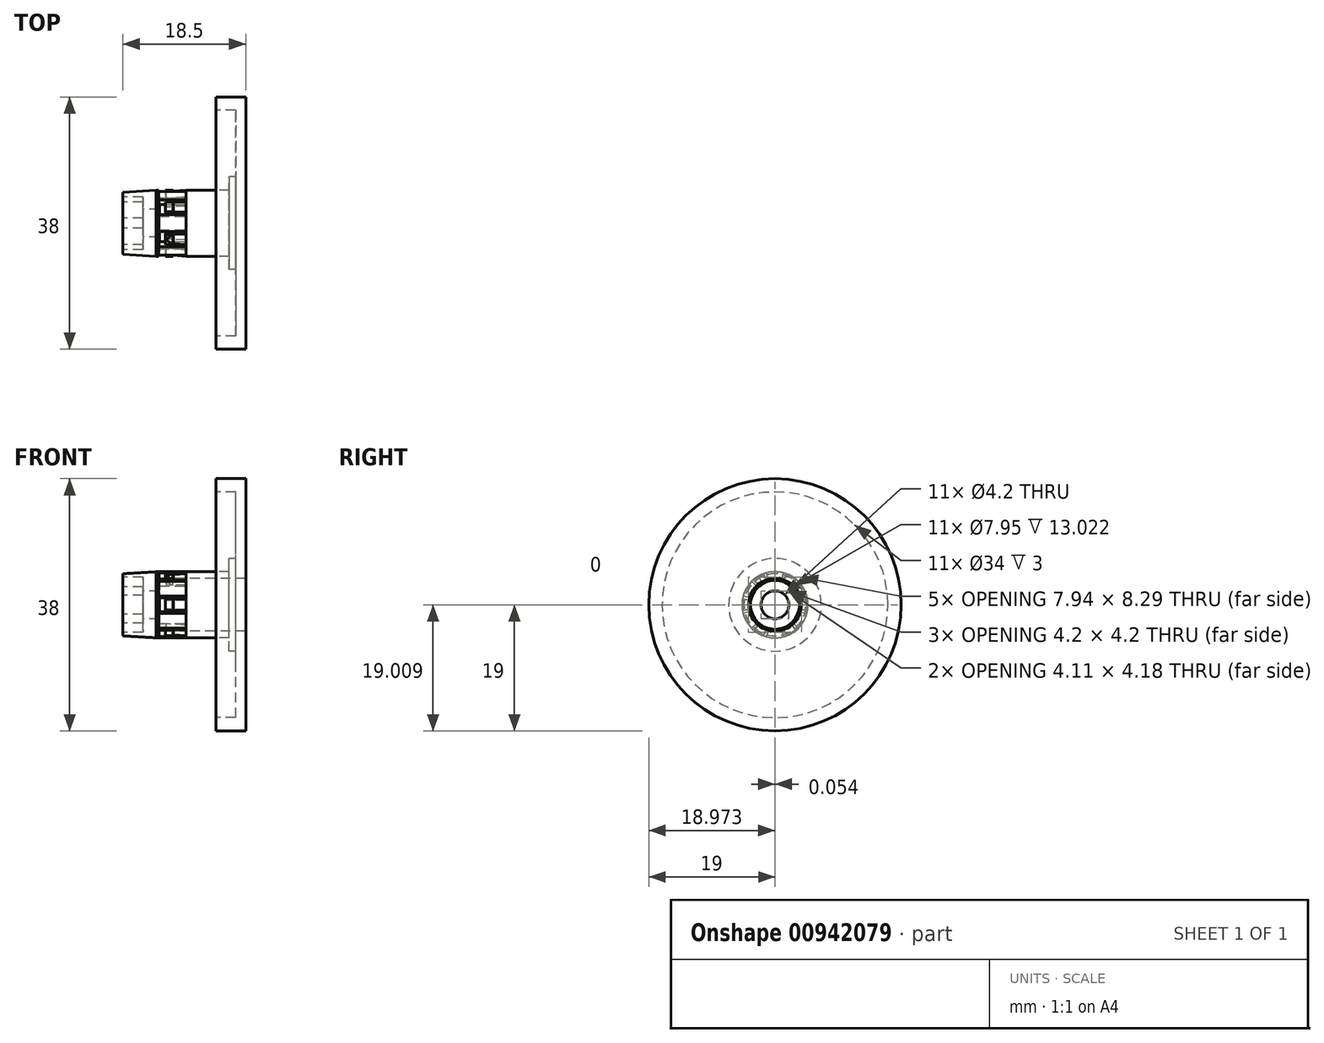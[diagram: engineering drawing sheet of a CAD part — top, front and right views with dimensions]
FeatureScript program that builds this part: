
annotation { "Feature Type Name" : "Feature", "Feature Type Description" : "" }
export const myFeature = defineFeature(function(context is Context, id is Id, definition is map)
    precondition{}
    {
        {
            var Q0;
            Q0=qCreatedBy(makeId("Top.planeOp"),FACE);
            var sketch = newSketch(context, id + "F0", { "sketchPlane" : qUnion([Q0])});
            skLineSegment(sketch, "E0", {"start": v(0, 19) * mm, "end": v(-4.5, 19) * mm});
            skLineSegment(sketch, "E1", {"start": v(-4.5, 19) * mm, "end": v(-4.5, 17) * mm});
            skLineSegment(sketch, "E2", {"start": v(-4.5, 17) * mm, "end": v(-1.5, 17) * mm});
            skLineSegment(sketch, "E3", {"start": v(-1.5, 17) * mm, "end": v(-1.5, 6.97) * mm});
            skLineSegment(sketch, "E4", {"start": v(-2.5, 4.97) * mm, "end": v(-18.5, 4.98) * mm});
            skLineSegment(sketch, "E5", {"start": v(-9, 3.97) * mm, "end": v(0, 3.97) * mm});
            skLineSegment(sketch, "E6", {"start": v(0, 19) * mm, "end": v(0, 3.97) * mm});
            skPoint(sketch, "E7.visualSharp", {"position": v(-1.5, 4.97) * mm});
            skLineSegment(sketch, "E8", {"start": v(-2.5, 4.97) * mm, "end": v(-2.5, 6.97) * mm});
            skLineSegment(sketch, "E9", {"start": v(-2.5, 6.97) * mm, "end": v(-1.5, 6.97) * mm});
            skLineSegment(sketch, "E10", {"start": v(-18.5, 2.1) * mm, "end": v(-13, 2.1) * mm});
            skLineSegment(sketch, "E11", {"start": v(-9, 3.97) * mm, "end": v(-13, 3.67) * mm});
            skLineSegment(sketch, "E12", {"start": v(-13, 3.67) * mm, "end": v(-13, 2.1) * mm});
            skLineSegment(sketch, "E13", {"start": v(-18.5, 2.1) * mm, "end": v(-18.5, 4.97) * mm});
            skLineSegment(sketch, "E14", {"start": v(-9, 3.97) * mm, "end": v(-9, 4.97) * mm});
            skLineSegment(sketch, "E15", {"start": v(-13, 3.67) * mm, "end": v(-13.1, 4.97) * mm});
            skLineSegment(sketch, "E16", {"start": v(0, 0) * mm, "end": v(12.8, 0) * mm, "construction": true});
            skLineSegment(sketch, "E17", {"start": v(-9, 4.97) * mm, "end": v(-12.1, 4.97) * mm});
            skLineSegment(sketch, "E18", {"start": v(-12.1, 4.97) * mm, "end": v(-12, 3.75) * mm});
            skLineSegment(sketch, "E19", {"start": v(-9, 4.97) * mm, "end": v(-10.92, 4.83) * mm});
            skLineSegment(sketch, "E20", {"start": v(-10.92, 4.83) * mm, "end": v(-10.93, 4.97) * mm});
            skSolve(sketch);
        }
        {
            var Q0;
            Q0=makeQuery(id+"F0.imprint","IMPRINT",FACE,{"disambiguationData":[TD([[makeQuery(id+"F0.imprint","IMPRINT",EDGE,{"derivedFrom":sQuery(id+"F0.wireOp",EDGE,"E0")}),1.0]])]});
            var Q1;
            Q1=makeQuery(id+"F0.imprint","IMPRINT",FACE,{"disambiguationData":[TD([[makeQuery(id+"F0.imprint","IMPRINT",EDGE,{"derivedFrom":sQuery(id+"F0.wireOp",EDGE,"E10")}),1.0]])]});
            var Q2;
            Q2=sQuery(id+"F0.wireOp",EDGE,"E16");
            revolve(context, id + "F1", {"surfaceOperationType" : NewSurfaceOperationType.NEW, "entities" : qUnion([Q0, Q1]), "axis" : qUnion([Q2]), "revolveType" : RevolveType.FULL});
        }
        {
            var Q0;
            {var subQ0=sQuery(id+"F0.wireOp",EDGE,"E18");Q0=makeQuery(id+"F0.imprint","IMPRINT",FACE,{"disambiguationData":[TD([[makeQuery(id+"F0.imprint","IMPRINT",EDGE,{"derivedFrom":subQ0}),1.0]])]});}
            var Q1;
            Q1=sQuery(id+"F0.wireOp",EDGE,"E16");
            revolve(context, id + "F2", {"operationType" : NewBodyOperationType.ADD, "surfaceOperationType" : NewSurfaceOperationType.NEW, "entities" : qUnion([Q0]), "axis" : qUnion([Q1]), "revolveType" : RevolveType.SYMMETRIC, "angle" : 20 * degree});
        }
        {
            var Q0;
            Q0=makeQuery(id+"F1.opRevolve","SWEPT_FACE",FACE,{"disambiguationData":[OSD([sQuery(id+"F0.wireOp",EDGE,"E14")])]});
            var sketch = newSketch(context, id + "F3", { "sketchPlane" : qUnion([Q0])});
            skLineSegment(sketch, "E21", {"start": v(-3.84, -1.03) * mm, "end": v(-4.8, -1.29) * mm});
            skLineSegment(sketch, "E22", {"start": v(-2.81, -2.81) * mm, "end": v(-3.52, -3.52) * mm});
            skPoint(sketch, "E23", {"position": v(0, 0) * mm});
            skArc(sketch, "E24", {"start": v(-2.81, -2.81) * mm, "mid": v(-3.44, -1.99) * mm, "end": v(-3.84, -1.03) * mm});
            skArc(sketch, "E25", {"start": v(-3.52, -3.52) * mm, "mid": v(-4.3, -2.49) * mm, "end": v(-4.8, -1.29) * mm});
            skSolve(sketch);
        }
        {
            var Q0;
            Q0=makeQuery(id+"F3.imprint","IMPRINT",FACE,{"disambiguationData":[TD([[makeQuery(id+"F3.imprint","IMPRINT",EDGE,{"derivedFrom":sQuery(id+"F3.wireOp",EDGE,"E21")}),1.0]])]});
            extrude(context, id + "F4", {"entities" : qUnion([Q0]), "operationType" : NewBodyOperationType.ADD, "endBound" : BoundingType.UP_TO_NEXT, "depth" : 25 * mm, "offsetDistance" : 25 * mm});
        }
        {
            var Q0;
            Q0=makeQuery(id+"F1.opRevolve","SWEPT_EDGE",EDGE,{"disambiguationData":[OSD([sQuery(id+"F0.wireOp",EDGE,"E4"),sQuery(id+"F0.wireOp",EDGE,"E13")])]});
            chamfer(context, id + "F5", {"entities" : qUnion([Q0]), "chamferType" : ChamferType.TWO_OFFSETS, "width1" : .3 * mm, "oppositeDirection" : false, "width2" : 5 * mm, "tangentPropagation" : true});
        }
        {
            var Q0;
            Q0=makeQuery(id+"F1.opRevolve","SWEPT_BODY",BODY,{"disambiguationData":[OSD([sQuery(id+"F0.wireOp",EDGE,"E0"),sQuery(id+"F0.wireOp",EDGE,"E1"),sQuery(id+"F0.wireOp",EDGE,"E2"),sQuery(id+"F0.wireOp",EDGE,"E3"),sQuery(id+"F0.wireOp",EDGE,"E4"),sQuery(id+"F0.wireOp",EDGE,"E5"),sQuery(id+"F0.wireOp",EDGE,"E6"),sQuery(id+"F0.wireOp",EDGE,"E8"),sQuery(id+"F0.wireOp",EDGE,"E9"),sQuery(id+"F0.wireOp",EDGE,"E14")])]});
            var Q1;
            Q1=sQuery(id+"F0.wireOp",EDGE,"E16");
            circularPattern(context, id + "F6", {"entities" : qUnion([Q0]), "axis" : qUnion([Q1]), "angle" : 360 * degree, "instanceCount" : 6, "equalSpace" : true, "isCentered" : true});
        }
        {
            var Q0;
            Q0=makeQuery(id+"F1.opRevolve","SWEPT_FACE",FACE,{"disambiguationData":[OSD([sQuery(id+"F0.wireOp",EDGE,"E13")])]});
            var sketch = newSketch(context, id + "F7", { "sketchPlane" : qUnion([Q0])});
            skCircle(sketch, "E26.cCircle", {"center": v(0, 0) * mm, "radius": 3.65 * mm, "construction": true});
            skLineSegment(sketch, "E26.0", {"start": v(3.97, -1.41) * mm, "end": v(0.76, -4.15) * mm});
            skLineSegment(sketch, "E26.1", {"start": v(0.76, -4.15) * mm, "end": v(-3.2, -2.73) * mm});
            skLineSegment(sketch, "E26.2", {"start": v(-3.2, -2.73) * mm, "end": v(-3.97, 1.41) * mm});
            skLineSegment(sketch, "E26.3", {"start": v(-3.97, 1.41) * mm, "end": v(-0.76, 4.15) * mm});
            skLineSegment(sketch, "E26.4", {"start": v(-0.76, 4.15) * mm, "end": v(3.2, 2.73) * mm});
            skLineSegment(sketch, "E26.5", {"start": v(3.2, 2.73) * mm, "end": v(3.97, -1.41) * mm});
            skPoint(sketch, "E26.0.midPoint", {"position": v(2.37, -2.78) * mm});
            skSolve(sketch);
        }
        {
            var Q0;
            Q0=makeQuery(id+"F7.imprint","IMPRINT",FACE,{"disambiguationData":[TD([[makeQuery(id+"F7.imprint","IMPRINT",EDGE,{"derivedFrom":sQuery(id+"F7.wireOp",EDGE,"E26.0")}),-1.0]])]});
            extrude(context, id + "F8", {"entities" : qUnion([Q0]), "operationType" : NewBodyOperationType.REMOVE, "oppositeDirection" : true, "depth" : 3 * mm, "offsetDistance" : 25 * mm});
        }
        {
            var Q0;
            Q0=makeQuery(id+"F1.opRevolve","SWEPT_EDGE",EDGE,{"disambiguationData":[OSD([sQuery(id+"F0.wireOp",EDGE,"E4"),sQuery(id+"F0.wireOp",EDGE,"E13")])]});
            var Q1;
            Q1=makeQuery(id+"F6.opPattern","COPY",EDGE,{"derivedFrom":makeQuery(id+"F4.opExtrude","CAP_EDGE",EDGE,{"disambiguationData":[OSD([sQuery(id+"F3.wireOp",EDGE,"E22")])],"isStart":false}),"instanceName":"-1"});
            var Q2;
            Q2=makeQuery(id+"F6.opPattern","COPY",EDGE,{"derivedFrom":makeQuery(id+"F4.opExtrude","CAP_EDGE",EDGE,{"disambiguationData":[OSD([sQuery(id+"F3.wireOp",EDGE,"E21")])],"isStart":false}),"instanceName":"-2"});
            var Q3;
            Q3=makeQuery(id+"F6.opPattern","COPY",EDGE,{"derivedFrom":makeQuery(id+"F4.opExtrude","CAP_EDGE",EDGE,{"disambiguationData":[OSD([sQuery(id+"F3.wireOp",EDGE,"E21")])],"isStart":false}),"instanceName":"-1"});
            var Q4;
            Q4=makeQuery(id+"F4.opExtrude","CAP_EDGE",EDGE,{"disambiguationData":[OSD([sQuery(id+"F3.wireOp",EDGE,"E22")])],"isStart":false});
            var Q5;
            Q5=makeQuery(id+"F4.opExtrude","CAP_EDGE",EDGE,{"disambiguationData":[OSD([sQuery(id+"F3.wireOp",EDGE,"E21")])],"isStart":false});
            var Q6;
            Q6=makeQuery(id+"F6.opPattern","COPY",EDGE,{"derivedFrom":makeQuery(id+"F4.opExtrude","CAP_EDGE",EDGE,{"disambiguationData":[OSD([sQuery(id+"F3.wireOp",EDGE,"E22")])],"isStart":false}),"instanceName":"-5"});
            var Q7;
            Q7=makeQuery(id+"F6.opPattern","COPY",EDGE,{"derivedFrom":makeQuery(id+"F4.opExtrude","CAP_EDGE",EDGE,{"disambiguationData":[OSD([sQuery(id+"F3.wireOp",EDGE,"E21")])],"isStart":false}),"instanceName":"-5"});
            var Q8;
            Q8=makeQuery(id+"F6.opPattern","COPY",EDGE,{"derivedFrom":makeQuery(id+"F4.opExtrude","CAP_EDGE",EDGE,{"disambiguationData":[OSD([sQuery(id+"F3.wireOp",EDGE,"E22")])],"isStart":false}),"instanceName":"-4"});
            var Q9;
            Q9=makeQuery(id+"F6.opPattern","COPY",EDGE,{"derivedFrom":makeQuery(id+"F4.opExtrude","CAP_EDGE",EDGE,{"disambiguationData":[OSD([sQuery(id+"F3.wireOp",EDGE,"E21")])],"isStart":false}),"instanceName":"-4"});
            var Q10;
            Q10=makeQuery(id+"F6.opPattern","COPY",EDGE,{"derivedFrom":makeQuery(id+"F2.opRevolve","CAP_EDGE",EDGE,{"disambiguationData":[OSD([sQuery(id+"F0.wireOp",EDGE,"E18")])],"isStart":true}),"instanceName":"-4"});
            var Q11;
            Q11=makeQuery(id+"F6.opPattern","COPY",EDGE,{"derivedFrom":makeQuery(id+"F2.opRevolve","CAP_EDGE",EDGE,{"disambiguationData":[OSD([sQuery(id+"F0.wireOp",EDGE,"E18")])],"isStart":false}),"instanceName":"-4"});
            var Q12;
            Q12=makeQuery(id+"F6.opPattern","COPY",EDGE,{"derivedFrom":makeQuery(id+"F4.opExtrude","CAP_EDGE",EDGE,{"disambiguationData":[OSD([sQuery(id+"F3.wireOp",EDGE,"E22")])],"isStart":false}),"instanceName":"-3"});
            var Q13;
            Q13=makeQuery(id+"F6.opPattern","COPY",EDGE,{"derivedFrom":makeQuery(id+"F4.opExtrude","CAP_EDGE",EDGE,{"disambiguationData":[OSD([sQuery(id+"F3.wireOp",EDGE,"E21")])],"isStart":false}),"instanceName":"-3"});
            var Q14;
            Q14=makeQuery(id+"F6.opPattern","COPY",EDGE,{"derivedFrom":makeQuery(id+"F4.opExtrude","CAP_EDGE",EDGE,{"disambiguationData":[OSD([sQuery(id+"F3.wireOp",EDGE,"E22")])],"isStart":false}),"instanceName":"-2"});
            chamfer(context, id + "F9", {"entities" : qUnion([Q0, Q1, Q2, Q3, Q4, Q5, Q6, Q7, Q8, Q9, Q10, Q11, Q12, Q13, Q14]), "width" : 1 * mm, "tangentPropagation" : true});
        }
    });
